# Revit family: Divider_Curtain-PSS-4040XL-Top_Roll
name_source: partatom
category: Specialty Equipment
revit_build: Autodesk Revit 2017 (Build: 20170816_0615(x64)
units: mm (PartAtom-declared; Revit-internal decimal feet)

## family parameters
Always vertical = Yes
Cut with Voids When Loaded = No
OmniClass Number = 23.40.50.34.17
OmniClass Title = Gymnasium Dividers
Part Type = Normal
Room Calculation Point = No
Round Connector Dimension = Use Diameter
Shared = No
Work Plane-Based = No

## types (1)
- 74'-0" x 23'-7 7/8"
    Assembly Code = E1020900
    Attachment Height = 24' - 6"
    BIM Version = v3.1
    Bridge Pipe Requirement = Bridge Pipe required when structure exceeds 14' span
    CSI MasterFormat = 11 66 53
    Carrier Center Spacing = 12' - 0"
    Curtain Lower Material = Vinyl Coated Fabric - Performance Sports Systems - C04 Royal Blue
    Curtain Lower Material Height = 8' - 0"
    Curtain Upper Material = Vinyl Mesh - Performance Sports Systems - M01 White
    Description = Top-Roll Divider Curtain
    Dim End Carriers to First Carriers = 10' - 0"
    Height = 23' - 7 7/8"
    Installation Limitations = 36' Maximum Height to Centerline of Drive / Roller Tube
    Length = 74' - 0"
    Manufacturer = Performance Sports Systems
    Maximum Size Limitations = 36' High x 130' Long (Requires 2 Motors)
    Model = 4040XL
    Motor Location Note = Motor can be located at either end of curtain
    Product Page URL = http://www.perfsports.com
    Single Motor Limitation = Single Motor will accommodate up to 325 lb. curtain
    Superstructure Finish = Powder Coat - Performance Sports Systems - Black
    URL = http://www.perfsports.com

## geometry (parser evidence)
native form markers: Blend x107, Sweep x9
no freeform markers — native parametric forms only
